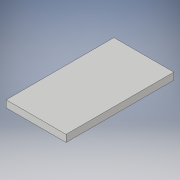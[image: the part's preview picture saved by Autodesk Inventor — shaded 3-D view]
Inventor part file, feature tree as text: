
AUTODESK INVENTOR PART (.ipt)
format: ipt  version: 2019.4 (Build 234330000, 330)  size: 93,696 bytes
history: native  units: in
note: dims shown in document units (in); Inventor stores cm internally (conversion verified against a paired STEP export)
features: extrude x1, sketch x1
ambient origin geometry x8: Origin, YZ Plane, XZ Plane, XY Plane, X Axis, Y Axis, Z Axis, Center Point
bodies: Solid1 (feature_tree)
feature tree (2):
  extrude  "Extrusion1"  Depth=8.5039in
  sketch  "Sketch1"  dims[d0=4.7244in d1=8.5039in d2=0.5512in d3=0.0in]
